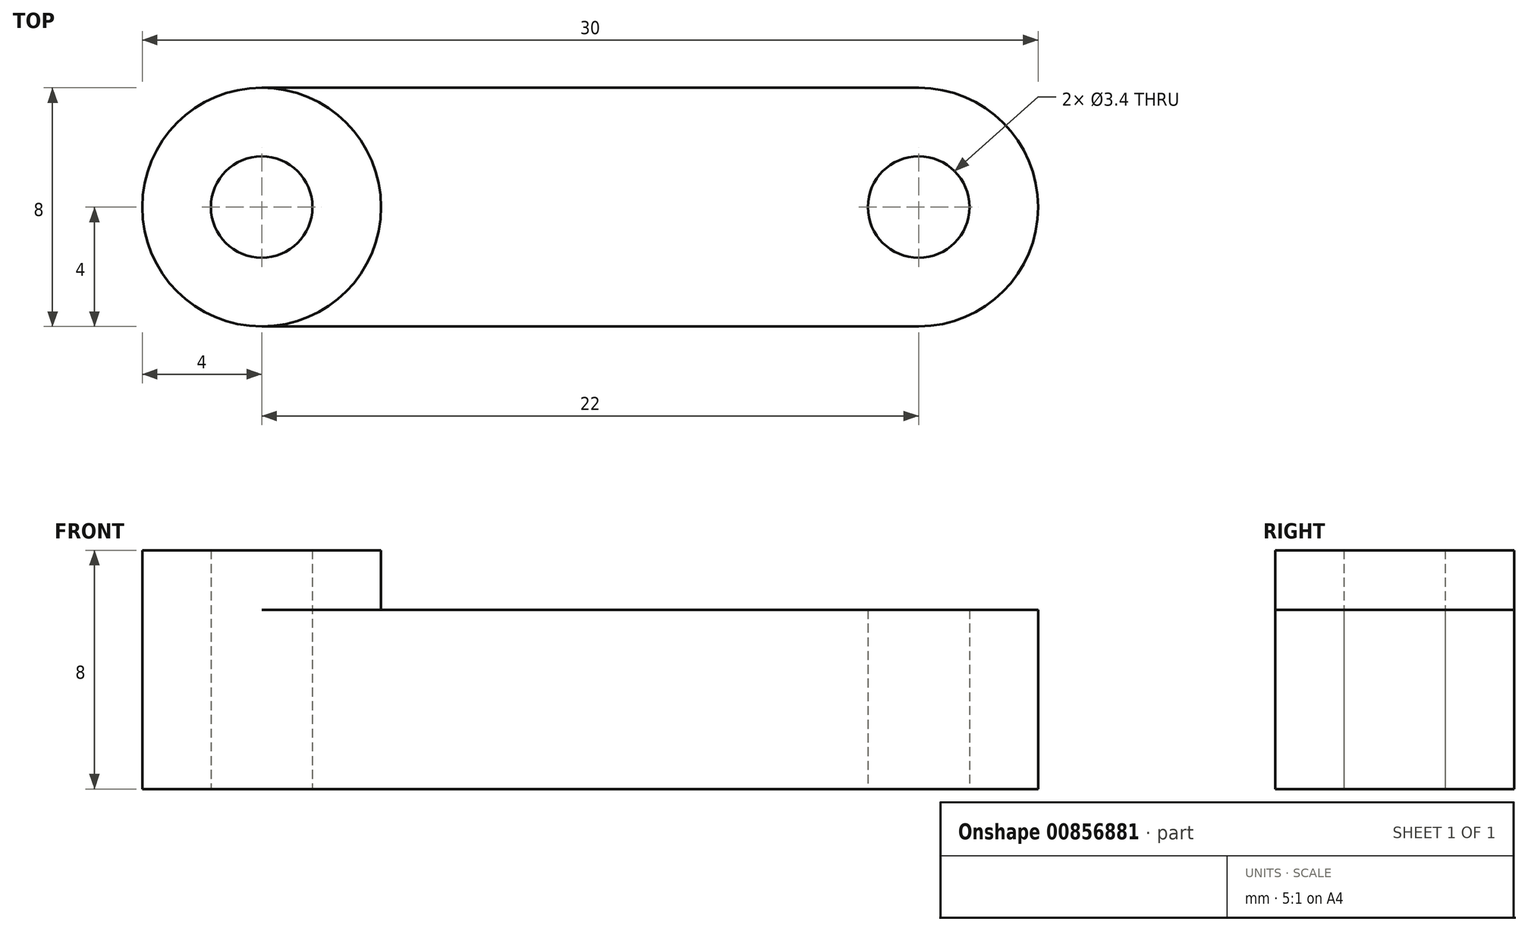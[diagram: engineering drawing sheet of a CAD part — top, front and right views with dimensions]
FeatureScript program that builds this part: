
annotation { "Feature Type Name" : "Feature", "Feature Type Description" : "" }
export const myFeature = defineFeature(function(context is Context, id is Id, definition is map)
    precondition{}
    {
        {
            var Q0;
            Q0=qCreatedBy(makeId("Top.planeOp"),FACE);
            var sketch = newSketch(context, id + "F0", { "sketchPlane" : qUnion([Q0])});
            skLineSegment(sketch, "E0.bottom", {"start": v(15, -4) * mm, "end": v(-15, -4) * mm});
            skLineSegment(sketch, "E0.top", {"start": v(15, 4) * mm, "end": v(-15, 4) * mm});
            skLineSegment(sketch, "E0.left", {"start": v(15, -4) * mm, "end": v(15, 4) * mm});
            skLineSegment(sketch, "E0.right", {"start": v(-15, -4) * mm, "end": v(-15, 4) * mm});
            skPoint(sketch, "E0.middle", {"position": v(0, 0) * mm});
            skCircle(sketch, "E1", {"center": v(-11, 0) * mm, "radius": 1.7 * mm});
            skCircle(sketch, "E2", {"center": v(11, 0) * mm, "radius": 1.7 * mm});
            skSolve(sketch);
        }
        {
            var Q0;
            Q0 = qSketchRegion(id + "F0", true);
            extrude(context, id + "F1", {"entities" : qUnion([Q0]), "depth" : 6 * mm, "offsetDistance" : 25 * mm});
        }
        {
            var Q0;
            Q0=makeQuery(id+"F1.opExtrude","CAP_FACE",FACE,{"disambiguationData":[OSD([sQuery(id+"F0.wireOp",EDGE,"E0.bottom"),sQuery(id+"F0.wireOp",EDGE,"E0.top"),sQuery(id+"F0.wireOp",EDGE,"E0.left"),sQuery(id+"F0.wireOp",EDGE,"E0.right"),sQuery(id+"F0.wireOp",EDGE,"E1"),sQuery(id+"F0.wireOp",EDGE,"E2")])],"isStart":false});
            var sketch = newSketch(context, id + "F2", { "sketchPlane" : qUnion([Q0])});
            skLineSegment(sketch, "E3.bottom", {"start": v(-15, -4) * mm, "end": v(-7, -4) * mm});
            skLineSegment(sketch, "E3.top", {"start": v(-15, 4) * mm, "end": v(-7, 4) * mm});
            skLineSegment(sketch, "E3.left", {"start": v(-15, -4) * mm, "end": v(-15, 4) * mm});
            skLineSegment(sketch, "E3.right", {"start": v(-7, -4) * mm, "end": v(-7, 4) * mm});
            skPoint(sketch, "E3.middle", {"position": v(-11, 0) * mm});
            skSolve(sketch);
        }
        {
            var Q0;
            Q0=makeQuery(id+"F2.imprint","IMPRINT",FACE,{"disambiguationData":[TD([[makeQuery(id+"F2.imprint","IMPRINT",EDGE,{"derivedFrom":sQuery(id+"F2.wireOp",EDGE,"E3.bottom")}),-1.0]])]});
            extrude(context, id + "F3", {"entities" : qUnion([Q0]), "operationType" : NewBodyOperationType.ADD, "depth" : 2 * mm, "offsetDistance" : 25 * mm});
        }
        {
            var Q0;
            Q0=makeQuery(id+"F1.opExtrude","SWEPT_EDGE",EDGE,{"disambiguationData":[OSD([sQuery(id+"F0.wireOp",EDGE,"E0.top"),sQuery(id+"F0.wireOp",EDGE,"E0.right")])]});
            var Q1;
            Q1=makeQuery(id+"F1.opExtrude","SWEPT_EDGE",EDGE,{"disambiguationData":[OSD([sQuery(id+"F0.wireOp",EDGE,"E0.bottom"),sQuery(id+"F0.wireOp",EDGE,"E0.right")])]});
            var Q2;
            Q2=makeQuery(id+"F3.boolean.opBoolean","COPY",EDGE,{"derivedFrom":makeQuery(id+"F3.opExtrude","CAP_EDGE",EDGE,{"disambiguationData":[OSD([sQuery(id+"F2.wireOp",EDGE,"E3.right")])],"isStart":true})});
            var Q3;
            Q3=makeQuery(id+"F1.opExtrude","SWEPT_EDGE",EDGE,{"disambiguationData":[OSD([sQuery(id+"F0.wireOp",EDGE,"E0.top"),sQuery(id+"F0.wireOp",EDGE,"E0.left")])]});
            var Q4;
            Q4=makeQuery(id+"F1.opExtrude","SWEPT_EDGE",EDGE,{"disambiguationData":[OSD([sQuery(id+"F0.wireOp",EDGE,"E0.bottom"),sQuery(id+"F0.wireOp",EDGE,"E0.left")])]});
            var Q5;
            Q5=makeQuery(id+"F3.opExtrude","SWEPT_EDGE",EDGE,{"disambiguationData":[OSD([sQuery(id+"F0.wireOp",EDGE,"E0.bottom"),sQuery(id+"F2.wireOp",EDGE,"E3.bottom"),sQuery(id+"F2.wireOp",EDGE,"E3.right")])]});
            var Q6;
            Q6=makeQuery(id+"F3.opExtrude","SWEPT_EDGE",EDGE,{"disambiguationData":[OSD([sQuery(id+"F0.wireOp",EDGE,"E0.top"),sQuery(id+"F2.wireOp",EDGE,"E3.top"),sQuery(id+"F2.wireOp",EDGE,"E3.right")])]});
            fillet(context, id + "F4", {"entities" : qUnion([Q0, Q1, Q2, Q3, Q4, Q5, Q6]), "radius" : 4 * mm, "tangentPropagation" : true, "allowEdgeOverflow" : false});
        }
    });
